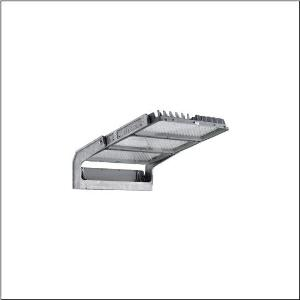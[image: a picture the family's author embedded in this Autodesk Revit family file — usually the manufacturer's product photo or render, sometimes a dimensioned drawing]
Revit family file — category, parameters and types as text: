
# Revit family: floodlight_fl_11_maxi_pro___rs08_5xa779128l02fb_6b31
name_source: partatom
category: Lighting Fixtures
units: mm (PartAtom-declared; Revit-internal decimal feet)

## family parameters
Cut with Voids When Loaded = No
Host = Face
Light Source = No
Part Type = Normal
Room Calculation Point = No
Round Connector Dimension = Use Diameter
Shared = No

## types (1)
- --- (1 x LED, 155960 lm, 1368.3 W, 5700K)
    Apparent Load = 1368 VA
    CIE Flux Codes = 70 87 98 100 100
    Color Rendering = 80
    Color Temperature = 5700K
    Default Elevation = 1800 mm
    Description = Floodlight FL 11  maxi  pro floodlight; light control with lens of PMMA; cover panel of toughened safety glass, transparent; light distribution: RS08, rotationally symmetric direct distribution, LED; colour temperature: 5700K, rated luminous flux: 155.960lm, colour rendering: CRI > 80, light colour: 857; luminous efficacy: 114lm/W; brightness control: DALI 2; with terminal, 5-pole, max. 2.5mm², mains connection: 220..240V/380..400V AC, 50/60Hz, surge voltage resistance: line to ground: 10kV, LED service life up to 100,000h L90. Typical operating time: 1000h per year., ECG replaceable separately, LED unit replaceable without ESD environment, dustproof LED module, dimming range 10..100%; 1368W floodlight with 3x LED unit of diecast aluminium, coated grey; length: 1.003mm / width: 651mm / height: 338mm; mounting bracket, of diecast aluminium, uncoated, natural, equipment: Power, protection rating (complete): IP66; insulation class (complete): insulation class I (protective earthing); certification: CE, ENEC, VDE; ball protection: ball impact resistant, only for outdoor installations in the designated locations, permissible operating ambient temperature: -45..+55°C, permissible storage temperature: -40..+85°Cpackaging unit: 1 piece

Light Distribution: RS08
    Height = 320 mm
    Lamp = 1 x LED
    Lamp Light Flux = 155960 lm
    Lamp Power = 1368.3 W
    Lamp count = 1
    Length = 1002 mm
    Luminous efficacy = 114 lm/W
    Manufacturer = Siteco
    ModVariant = No
    Model = 5XA779128L02FB
    Mounting Place = Ceiling
    Mounting Type = Surface mounted
    Number of Poles = 1
    OnlyDefault = Yes
    Power Factor = 1
    Product Name = Floodlight FL 11 maxi pro | RS08
    Product group = floodlight | ceiling mounted
    ProductGroupID = 303
    Protection Class = Protection class I
    Protection Degree = IP 66
    RLX_Detail_Level = 1
    RLX_Emergency_Light_Flux = 0 lm
    RLX_Emergency_Type = 0
    RLX_Emergency_Type_DB = No
    RlxData = <blob elided: 40345 chars, md5=5c3d00ed>
    Socket = socket
    Standby Power = 0 W
    System Light Flux = 155960 lm
    System Power = 1368 W
    Type Comments = factory setting: luminous flux: 100 % | dim-lin: 254 | 935 mA
    Type Image = l_1356210.jpg
    URL = http://relux.com
    VarID = @adj_039935
    Voltage = 0 V
    Weight = 0.00 kg
    Width = 655 mm

## geometry (parser evidence)
native form markers: Blend x4, Sweep x11
no freeform markers — native parametric forms only
